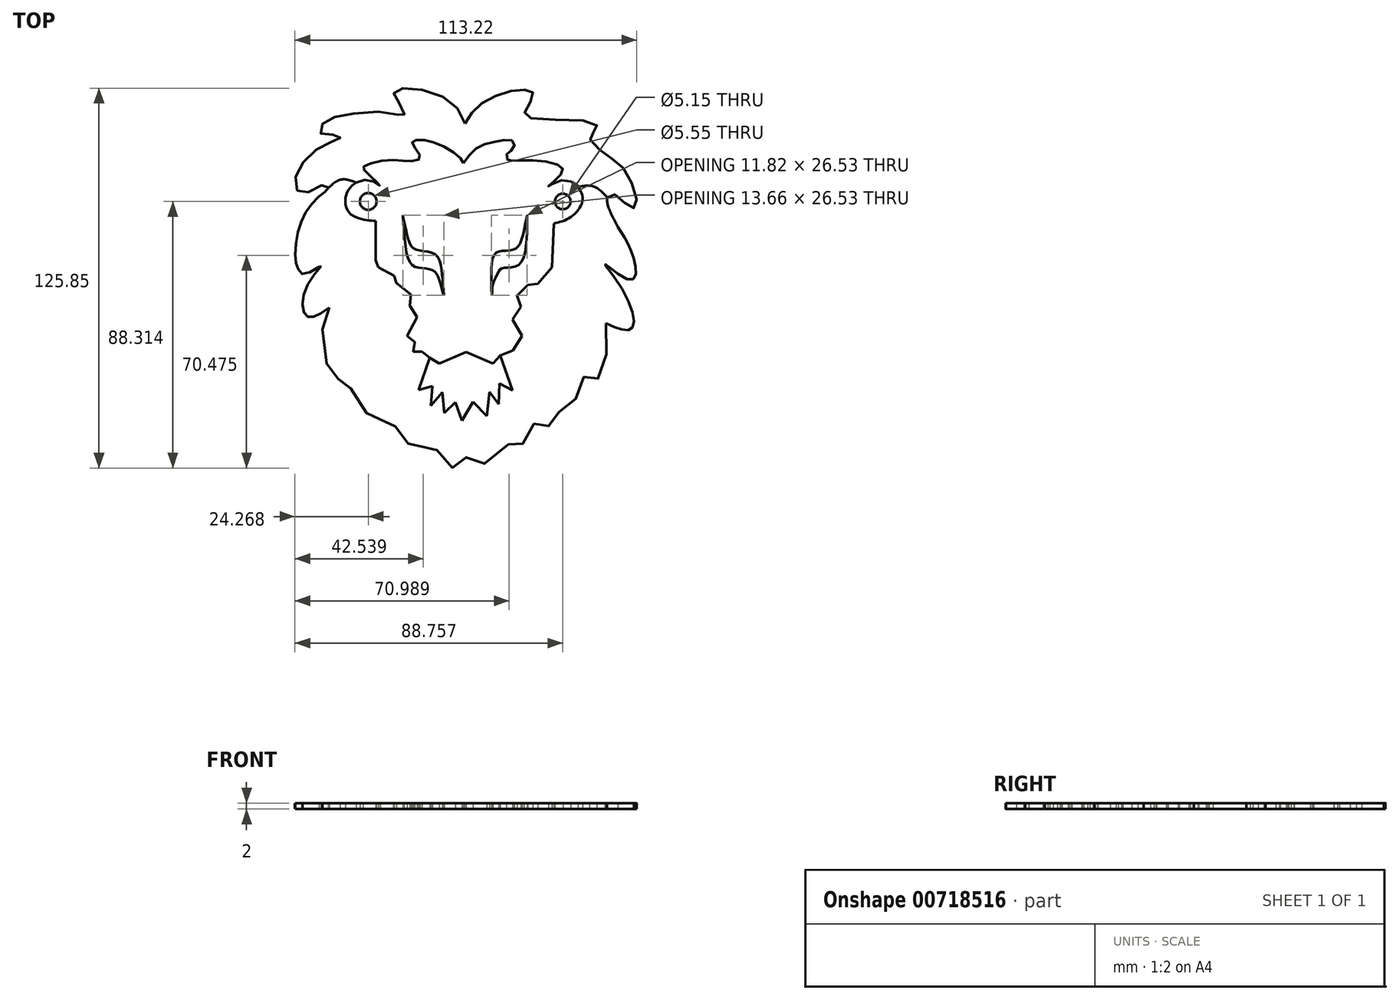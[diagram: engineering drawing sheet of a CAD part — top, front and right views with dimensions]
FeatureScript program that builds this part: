
annotation { "Feature Type Name" : "Feature", "Feature Type Description" : "" }
export const myFeature = defineFeature(function(context is Context, id is Id, definition is map)
    precondition{}
    {
        {
            var Q0;
            Q0=qCreatedBy(makeId("Top.planeOp"),FACE);
            var sketch = newSketch(context, id + "F0", { "sketchPlane" : qUnion([Q0])});
            skLineSegment(sketch, "E0", {"start": v(-53.78, -25.28) * mm, "end": v(-57.52, -35.88) * mm});
            skLineSegment(sketch, "E1", {"start": v(-57.52, -35.88) * mm, "end": v(-52.94, -34.64) * mm});
            skLineSegment(sketch, "E2", {"start": v(-52.94, -34.64) * mm, "end": v(-53.36, -41.09) * mm});
            skLineSegment(sketch, "E3", {"start": v(-53.36, -41.09) * mm, "end": v(-49.61, -36.72) * mm});
            skLineSegment(sketch, "E4", {"start": v(-49.61, -36.72) * mm, "end": v(-49, -43.58) * mm});
            skLineSegment(sketch, "E5", {"start": v(-49, -43.58) * mm, "end": v(-45.25, -40.05) * mm});
            skLineSegment(sketch, "E6", {"start": v(-45.25, -40.05) * mm, "end": v(-43.17, -46.08) * mm});
            skLineSegment(sketch, "E7", {"start": v(-43.17, -46.08) * mm, "end": v(-39.42, -39.84) * mm});
            skLineSegment(sketch, "E8", {"start": v(-39.42, -39.84) * mm, "end": v(-34.84, -44.62) * mm});
            skLineSegment(sketch, "E9", {"start": v(-34.84, -44.62) * mm, "end": v(-34.01, -36.5) * mm});
            skLineSegment(sketch, "E10", {"start": v(-34.01, -36.5) * mm, "end": v(-30.9, -40.67) * mm});
            skLineSegment(sketch, "E11", {"start": v(-30.9, -40.67) * mm, "end": v(-30.68, -33.8) * mm});
            skLineSegment(sketch, "E12", {"start": v(-30.68, -33.8) * mm, "end": v(-26.32, -36.1) * mm});
            skLineSegment(sketch, "E13", {"start": v(-26.32, -36.1) * mm, "end": v(-30.48, -24.44) * mm});
            skLineSegment(sketch, "E14", {"start": v(-30.48, -24.44) * mm, "end": v(-32.76, -27.15) * mm});
            skLineSegment(sketch, "E15", {"start": v(-32.76, -27.15) * mm, "end": v(-41.7, -23.4) * mm});
            skLineSegment(sketch, "E16", {"start": v(-41.7, -23.4) * mm, "end": v(-50.65, -27.15) * mm});
            skLineSegment(sketch, "E17", {"start": v(-50.65, -27.15) * mm, "end": v(-53.78, -25.28) * mm});
            skLineSegment(sketch, "E18", {"start": v(-30.48, -24.44) * mm, "end": v(-26.18, -22.9) * mm});
            skLineSegment(sketch, "E19", {"start": v(-26.18, -22.9) * mm, "end": v(-23.2, -18) * mm});
            skLineSegment(sketch, "E20", {"start": v(-23.2, -18) * mm, "end": v(-26.32, -12.59) * mm});
            skLineSegment(sketch, "E21", {"start": v(-26.32, -12.59) * mm, "end": v(-23.61, -8.43) * mm});
            skLineSegment(sketch, "E22", {"start": v(-23.61, -8.43) * mm, "end": v(-24.86, -4.68) * mm});
            skLineSegment(sketch, "E23", {"start": v(-24.86, -4.68) * mm, "end": v(-21.32, -1.14) * mm});
            skLineSegment(sketch, "E24", {"start": v(-21.32, -1.14) * mm, "end": v(-18, -0.73) * mm});
            skLineSegment(sketch, "E25", {"start": v(-18, -0.73) * mm, "end": v(-13.2, 4.68) * mm});
            skLineSegment(sketch, "E26", {"start": v(-13.2, 4.68) * mm, "end": v(-12.59, 19.24) * mm});
            skLineSegment(sketch, "E27", {"start": v(-53.78, -25.28) * mm, "end": v(-56.27, -23.2) * mm});
            skLineSegment(sketch, "E28", {"start": v(-56.27, -23.2) * mm, "end": v(-59.18, -23.2) * mm});
            skLineSegment(sketch, "E29", {"start": v(-59.18, -23.2) * mm, "end": v(-58.77, -20.07) * mm});
            skLineSegment(sketch, "E30", {"start": v(-58.77, -20.07) * mm, "end": v(-61.26, -18) * mm});
            skLineSegment(sketch, "E31", {"start": v(-61.26, -18) * mm, "end": v(-57.94, -11.75) * mm});
            skLineSegment(sketch, "E32", {"start": v(-57.94, -11.75) * mm, "end": v(-60.43, -8) * mm});
            skLineSegment(sketch, "E33", {"start": v(-60.43, -8) * mm, "end": v(-60.02, -4.26) * mm});
            skLineSegment(sketch, "E34", {"start": v(-60.02, -4.26) * mm, "end": v(-64.8, -0.52) * mm});
            skLineSegment(sketch, "E35", {"start": v(-64.8, -0.52) * mm, "end": v(-65.63, 1.98) * mm});
            skLineSegment(sketch, "E36", {"start": v(-65.63, 1.98) * mm, "end": v(-70.83, 4.68) * mm});
            skLineSegment(sketch, "E37", {"start": v(-70.83, 4.68) * mm, "end": v(-71.67, 6.97) * mm});
            skLineSegment(sketch, "E38", {"start": v(-71.67, 6.97) * mm, "end": v(-71.67, 20.07) * mm});
            skFitSpline(sketch, "E39", {"points": [v(-12.59, 19.24) * mm, v(-7.39, 21.11) * mm, v(-3.22, 26.32) * mm, v(-4.68, 31.3) * mm, v(-10.09, 33.6) * mm, v(-14.46, 31.52) * mm, v(-11.55, 34.22) * mm, v(-9.67, 37.34) * mm, v(-16.12, 39.84) * mm, v(-26.1, 40.05) * mm, v(-27.98, 40.25) * mm, v(-28.19, 42.33) * mm, v(-26.1, 44) * mm, v(-26.1, 46.5) * mm, v(-31.3, 46.5) * mm, v(-37.97, 44.41) * mm, v(-42.54, 39.21) * mm], "startDerivative": vector(78.27, 17.75) * mm, "endDerivative": vector(-54.6, -79.97) * mm});
            skFitSpline(sketch, "E40", {"points": [v(-42.54, 39.21) * mm, v(-44.41, 41.7) * mm, v(-51.7, 45.87) * mm, v(-57.52, 46.91) * mm, v(-59.6, 46.29) * mm, v(-57.94, 43.37) * mm, v(-57.1, 40.67) * mm, v(-60.43, 39.84) * mm, v(-66.67, 40.25) * mm, v(-74.79, 38.59) * mm, v(-75.83, 37.55) * mm, v(-73.75, 35.26) * mm, v(-70.2, 31.72) * mm, v(-72.91, 33.39) * mm, v(-78.11, 32.76) * mm, v(-81.44, 28.81) * mm, v(-80.61, 22.99) * mm, v(-75.41, 20.5) * mm, v(-71.67, 20.07) * mm], "startDerivative": vector(-28.53, 51.11) * mm, "endDerivative": vector(67.1, -4.16) * mm});
            skCircle(sketch, "E41", {"center": v(-74.16, 26.52) * mm, "radius": 2.78 * mm});
            skCircle(sketch, "E42", {"center": v(-9.67, 26.52) * mm, "radius": 2.57 * mm});
            skFitSpline(sketch, "E43", {"points": [v(-62.72, 21.95) * mm, v(-61.26, 15.5) * mm, v(-59.4, 11.13) * mm, v(-55.86, 10.09) * mm, v(-51.49, 8.63) * mm, v(-49.82, 3.22) * mm, v(-49.06, -4.58) * mm], "startDerivative": vector(7.8, -35.85) * mm, "endDerivative": vector(2.55, -42.14) * mm});
            skFitSpline(sketch, "E44", {"points": [v(-49.06, -4.58) * mm, v(-50.12, -0.98) * mm, v(-51.9, 3.02) * mm, v(-55.19, 4.3) * mm, v(-59.89, 5.73) * mm, v(-62.72, 21.95) * mm], "startDerivative": vector(-10.03, 21) * mm, "endDerivative": vector(-6.06, 64.92) * mm});
            skFitSpline(sketch, "E45", {"points": [v(-33.24, -4.58) * mm, v(-32.98, -1.57) * mm, v(-31.1, 3.02) * mm, v(-29.44, 4.47) * mm, v(-24.23, 5.51) * mm, v(-21.53, 21.95) * mm], "startDerivative": vector(5.06, 21.56) * mm, "endDerivative": vector(0.04, 63.52) * mm});
            skFitSpline(sketch, "E46", {"points": [v(-21.53, 21.95) * mm, v(-22.78, 15.91) * mm, v(-24.24, 11.96) * mm, v(-26.94, 10.3) * mm, v(-31.1, 9.88) * mm, v(-32.97, 7.39) * mm, v(-33.24, -4.58) * mm], "startDerivative": vector(-6.68, -34.02) * mm, "endDerivative": vector(0.33, -53.45) * mm});
            skFitSpline(sketch, "E47", {"points": [v(-42.13, 52.32) * mm, v(-37.76, 58.14) * mm, v(-28.4, 62.72) * mm, v(-20.9, 63.34) * mm, v(-19.45, 61.89) * mm, v(-22.16, 56.48) * mm, v(-21.32, 54.4) * mm, v(1.14, 52.32) * mm, v(0.94, 49.82) * mm, v(-0.73, 47.53) * mm, v(4.68, 42.13) * mm, v(11.55, 35.88) * mm, v(14.67, 25.28) * mm, v(13, 24.44) * mm, v(7.6, 28.81) * mm, v(5.1, 27.77) * mm, v(8.63, 18) * mm], "startDerivative": vector(52.91, 91.36) * mm, "endDerivative": vector(77.86, -146.02) * mm});
            skFitSpline(sketch, "E48", {"points": [v(8.63, 18) * mm, v(10.92, 14.25) * mm, v(13.2, 9.47) * mm, v(14.46, 1.98) * mm, v(11.75, 0.73) * mm, v(4.47, 5.72) * mm, v(10.5, -3.43) * mm, v(13.63, -14.67) * mm, v(11.34, -16.12) * mm, v(4.68, -13.83) * mm], "startDerivative": vector(25.53, -40.74) * mm, "endDerivative": vector(-63.34, 29.68) * mm});
            skFitSpline(sketch, "E49", {"points": [v(4.68, -13.83) * mm, v(4.68, -25.28) * mm, v(1.98, -32.14) * mm, v(-1.35, -31.52) * mm, v(-2.6, -31.52) * mm, v(-4.47, -36.72) * mm, v(-8.43, -42.54) * mm, v(-12.38, -43.79) * mm, v(-14.25, -47.74) * mm, v(-16.54, -48.78) * mm, v(-19.66, -47.12) * mm, v(-22.78, -53.57) * mm, v(-25.48, -55.23) * mm, v(-29.02, -53.98) * mm, v(-38.17, -61.68) * mm, v(-42.13, -58.14) * mm, v(-45.25, -61.68) * mm, v(-48.78, -58.98) * mm, v(-52.94, -54.6) * mm, v(-56.48, -54.4) * mm, v(-58.35, -55.65) * mm, v(-60.85, -53.78) * mm, v(-64.6, -47.74) * mm, v(-67.3, -49.4) * mm, v(-72.08, -43.17) * mm, v(-73.54, -43.58) * mm, v(-77.9, -40.88) * mm, v(-82.07, -31.1) * mm, v(-85.19, -32.76) * mm, v(-88.1, -26.52) * mm, v(-89.14, -13.63) * mm, v(-87.06, -8.63) * mm], "startDerivative": vector(14.1, -236.05) * mm, "endDerivative": vector(77.85, 128.92) * mm});
            skFitSpline(sketch, "E50", {"points": [v(-87.06, -8.63) * mm, v(-92.47, -11.75) * mm, v(-94.76, -11.34) * mm, v(-96, -7.6) * mm, v(-93.1, 0.94) * mm, v(-89.76, 5.3) * mm, v(-95.17, 2.4) * mm, v(-97.25, 3.85) * mm, v(-98.3, 7.18) * mm, v(-97.46, 16.33) * mm, v(-94.13, 24.03) * mm, v(-89.14, 29.23) * mm, v(-87.27, 31.1) * mm, v(-88.3, 32.14) * mm, v(-92.88, 30.06) * mm, v(-97.25, 29.64) * mm, v(-98.3, 34.43) * mm, v(-94.34, 41.09) * mm, v(-87.06, 46.08) * mm, v(-83.52, 47.33) * mm, v(-83.94, 48.78) * mm, v(-88.3, 48.37) * mm, v(-90.39, 50.24) * mm, v(-87.9, 53.36) * mm, v(-80.4, 55.44) * mm, v(-65.22, 55.65) * mm, v(-62.3, 54.6) * mm, v(-63.14, 58.14) * mm, v(-65.63, 61.47) * mm, v(-65, 63.34) * mm, v(-58.14, 63.76) * mm, v(-46.5, 59.4) * mm, v(-42.13, 52.32) * mm], "startDerivative": vector(-169.92, -119.23) * mm, "endDerivative": vector(77.88, -194.8) * mm});
            skFitSpline(sketch, "E51", {"points": [v(-78.11, 32.76) * mm, v(-83.1, 33.8) * mm, v(-87.27, 31.1) * mm], "startDerivative": vector(-10.3, 3.96) * mm, "endDerivative": vector(-8, -7.31) * mm});
            skFitSpline(sketch, "E52", {"points": [v(-4.68, 31.3) * mm, v(0.52, 31.52) * mm, v(5.1, 27.77) * mm], "startDerivative": vector(11.2, 2.3) * mm, "endDerivative": vector(8.39, -9.24) * mm});
            skSolve(sketch);
        }
        {
            var Q0;
            {var subQ3=sQuery(id+"F0.wireOp",EDGE,"E51");Q0=makeQuery(id+"F0.imprint","IMPRINT",FACE,{"disambiguationData":[TD([[makeQuery(id+"F0.imprint","IMPRINT",EDGE,{"derivedFrom":subQ3}),-1.0]])]});}
            var Q1;
            Q1=makeQuery(id+"F0.imprint","IMPRINT",FACE,{"disambiguationData":[TD([[makeQuery(id+"F0.imprint","IMPRINT",EDGE,{"derivedFrom":sQuery(id+"F0.wireOp",EDGE,"E0")}),1.0]])]});
            extrude(context, id + "F1", {"entities" : qUnion([Q0, Q1]), "depth" : 2 * mm, "offsetDistance" : 25 * mm});
        }
        {
            var Q0;
            Q0=makeQuery(id+"F0.imprint","IMPRINT",FACE,{"disambiguationData":[TD([[makeQuery(id+"F0.imprint","IMPRINT",EDGE,{"derivedFrom":sQuery(id+"F0.wireOp",EDGE,"E43")}),-1.0]])]});
            var Q1;
            Q1=makeQuery(id+"F0.imprint","IMPRINT",FACE,{"disambiguationData":[TD([[makeQuery(id+"F0.imprint","IMPRINT",EDGE,{"derivedFrom":sQuery(id+"F0.wireOp",EDGE,"E45")}),1.0]])]});
            var Q2;
            Q2=makeQuery(id+"F0.imprint","IMPRINT",FACE,{"disambiguationData":[TD([[makeQuery(id+"F0.imprint","IMPRINT",EDGE,{"derivedFrom":sQuery(id+"F0.wireOp",EDGE,"E41")}),1.0]])]});
            var Q3;
            Q3=makeQuery(id+"F0.imprint","IMPRINT",FACE,{"disambiguationData":[TD([[makeQuery(id+"F0.imprint","IMPRINT",EDGE,{"derivedFrom":sQuery(id+"F0.wireOp",EDGE,"E42")}),1.0]])]});
            extrude(context, id + "F2", {"entities" : qUnion([Q0, Q1, Q2, Q3]), "depth" : 2 * mm, "offsetDistance" : 25 * mm});
        }
        {
            var Q0;
            Q0=makeQuery(id+"F0.imprint","IMPRINT",FACE,{"disambiguationData":[TD([[makeQuery(id+"F0.imprint","IMPRINT",EDGE,{"derivedFrom":sQuery(id+"F0.wireOp",EDGE,"E0")}),-1.0]])]});
            extrude(context, id + "F3", {"entities" : qUnion([Q0]), "depth" : 2 * mm, "offsetDistance" : 25 * mm});
        }
        {
            var Q0;
            Q0=makeQuery(id+"F0.imprint","IMPRINT",FACE,{"disambiguationData":[TD([[makeQuery(id+"F0.imprint","IMPRINT",EDGE,{"derivedFrom":sQuery(id+"F0.wireOp",EDGE,"E14")}),-1.0]])]});
            extrude(context, id + "F4", {"entities" : qUnion([Q0]), "depth" : 2 * mm, "offsetDistance" : 25 * mm});
        }
    });
